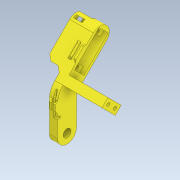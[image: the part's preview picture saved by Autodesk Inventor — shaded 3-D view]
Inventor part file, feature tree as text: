
AUTODESK INVENTOR PART (.ipt)
format: ipt  version: 2020 (Build 240168000, 168)  size: 848,384 bytes
history: native  units: mm
features: sketch x33, extrude x30, projected_geometry x17, reference x11, other x11, plane x4, chamfer x4, hole x3, split x2, boolean_combine x2, revolve x1, imported_body x1, fillet x1
ambient origin geometry x8: Origin, YZ Plane, XZ Plane, XY Plane, X Axis, Y Axis, Z Axis, Center Point
bodies: Solid1 (feature_tree), Solid2 (feature_tree), Solid3 (feature_tree), Solid4 (feature_tree), Solid5 (feature_tree), Solid6 (feature_tree)
feature tree (120):
  extrude  "Extrusion1"  Depth=70.0mm
  plane  "Work Plane1"
  extrude  "Extrusion2"  Depth=18.0mm
  extrude  "Extrusion3"  Depth=2.0mm TaperAngle=0.0deg
  extrude  "Extrusion4"  TaperAngle=0.0deg  [1 undecoded]
  extrude  "Extrusion5"  Depth=35.0mm TaperAngle=0.0deg
  extrude  "Extrusion12"  Depth=3.599976mm
  extrude  "Extrusion13"  Depth=0.15mm
  extrude  "Extrusion14"  Depth=0.15mm
  extrude  "Extrusion15"  Depth=15.9mm TaperAngle=0.0deg
  extrude  "Extrusion16"  Depth=5.0mm
  extrude  "Extrusion17"  Depth=53.0mm
  extrude  "Extrusion18"  Depth=37.3mm
  plane  "Work Plane2"
  extrude  "Extrusion19"  Depth=0.15mm
  hole  "Hole2"  [1 undecoded]
  plane  "Work Plane3"
  split  "Split1"
  extrude  "Extrusion20"  Depth=10.0mm
  extrude  "Extrusion21"  Depth=8.0mm
  extrude  "Extrusion22"  Depth=45.2mm TaperAngle=0.0deg
  plane  "Work Plane4"
  boolean_combine  "Combine1"
  split  "Split2"
  revolve  "Revolution1"  [1 undecoded]
  imported_body  "Base1"
  boolean_combine  "Combine2"
  hole  "Hole4"  [1 undecoded]
  extrude  "Extrusion30"  Depth=18.0mm
  extrude  "Extrusion31"  Depth=9.0mm
  extrude  "Extrusion33"  Depth=23.3mm
  extrude  "Extrusion34"  Depth=17.35mm TaperAngle=0.0deg
  chamfer  "Chamfer1"  Distance=10.0mm
  extrude  "Extrusion35"  Depth=3.0mm
  fillet  "Fillet3"  Radius=4.5mm
  extrude  "Extrusion36"  Depth=4.0mm
  extrude  "Extrusion37"  Depth=2.0mm
  extrude  "Extrusion38"  Depth=1.6mm TaperAngle=0.0deg
  extrude  "Extrusion39"  Depth=1.7mm TaperAngle=0.0deg
  extrude  "Extrusion40"  Depth=2.0mm
  chamfer  "Chamfer2"  Distance=12.899964mm
  extrude  "Extrusion42"  Depth=2.0mm
  extrude  "Extrusion43"  Depth=2.0mm
  extrude  "Extrusion48"  Depth=2.0mm
  extrude  "Extrusion49"  Depth=2.0mm
  chamfer  "Chamfer8"  Distance=30.143363mm
  chamfer  "Chamfer9"  Distance=124.5mm
  sketch  "Sketch1"  dims[d0=18.0mm d1=70.0mm]
  reference  "Reference1"
  sketch  "Sketch2"  dims[d2=70.0mm d3=18.0mm]
  reference  "Reference2"
  sketch  "Sketch3"  dims[d4=18.0mm d5=51.1mm d6=2.0mm d7=0.0mm d8=0.0mm]
  reference  "Reference3"
  reference  "Reference4"
  reference  "Reference5"
  reference  "Reference6"
  reference  "Reference7"
  reference  "Reference8"
  sketch  "Sketch4"  dims[d9=37.3mm d10=0.0mm]
  sketch  "Sketch5"  dims[d11=35.0mm d12=50.1mm d13=0.0mm]
  sketch  "Sketch12"  dims[d14=7.199887mm d15=3.599976mm]
  sketch  "Sketch14"  dims[d16=0.15mm d17=0.15mm]
  reference  "Reference12"
  reference  "Reference13"
  sketch  "Sketch15"  dims[d18=0.15mm d19=0.15mm]
  sketch  "Sketch16"  dims[d20=5.4mm d21=0.0mm d22=15.9mm d23=0.0mm]
  reference  "Reference14"
  sketch  "Sketch17"  dims[d24=5.0mm d25=0.0mm d78=3.85mm]
  sketch  "Sketch19"  dims[d79=10.925mm d80=53.0mm]
  sketch  "Sketch22"  dims[d81=53.0mm d82=37.3mm]
  projected_geometry  "Projected Loop1"
  sketch  "Sketch23"  dims[d83=40.0mm d84=0.0mm d86=0.15mm]
  sketch  "Sketch25"  dims[d87=0.15mm d88=4.0mm d89=0.0mm]
  sketch  "Sketch26"  dims[d90=20.0mm d91=0.0mm d92=10.0mm]
  sketch  "Sketch27"  dims[d93=4.0mm d94=0.0mm d95=8.0mm]
  sketch  "Sketch28"  dims[d96=18.0mm d97=45.2mm d98=0.0mm]
  sketch  "Sketch32"  dims[d99=12.7mm d100=0.3mm]
  projected_geometry  "Projected Loop2"
  projected_geometry  "Projected Loop3"
  sketch  "Sketch33"  dims[d101=12.7mm d102=0.3mm]
  hole  "Hole3"  [1 undecoded]
  sketch  "Sketch39"  dims[d103=10.0mm d104=0.0mm d109=18.0mm]
  projected_geometry  "Projected Loop15"
  projected_geometry  "Projected Loop16"
  projected_geometry  "Projected Loop17"
  sketch  "Sketch40"  dims[d111=31.0mm d112=9.0mm]
  projected_geometry  "Projected Loop18"
  sketch  "Sketch42"  dims[d113=9.0mm d114=23.3mm]
  projected_geometry  "Projected Loop20"
  sketch  "Sketch43"  dims[d115=23.3mm d116=17.35mm d117=0.0mm]
  projected_geometry  "Projected Loop21"
  projected_geometry  "Projected Loop22"
  sketch  "Sketch44"  dims[d118=15.0mm]
  sketch  "Sketch45"  dims[d119=4.0mm]
  projected_geometry  "Projected Loop23"
  sketch  "Sketch46"  dims[d120=8.0mm d121=10.0mm d122=0.0mm]
  sketch  "Sketch47"  dims[d132=3.0mm d133=3.0mm d134=4.5mm]
  projected_geometry  "Projected Loop24"
  sketch  "Sketch48"  dims[d135=4.5mm d136=4.0mm]
  sketch  "Sketch49"  dims[d137=4.0mm]
  projected_geometry  "Projected Loop25"
  sketch  "Sketch51"  dims[d138=3.0mm d139=6.0mm d140=4.0mm d141=2.0mm d142=90.0deg d143=56.75mm d144=0.0mm d146=0.765mm]
  projected_geometry  "Projected Loop27"
  sketch  "Sketch52"  dims[d147=1.6mm d148=0.0mm d149=1.6mm d150=0.0mm]
  projected_geometry  "Projected Loop28"
  sketch  "Sketch57"  dims[d151=0.765mm d152=1.7mm d153=0.0mm]
  projected_geometry  "Projected Loop33"
  sketch  "Sketch58"  dims[d167=45.0deg d170=3.4mm d171=6.0mm d172=4.0mm d173=2.0mm d174=90.0deg d175=8.0mm d176=0.0mm d234=1.309879mm d235=12.899964mm d236=16.829276mm d237=30.143363mm d238=6.142074mm d239=23.491994mm d240=30.143363mm d241=124.5mm d242=0.0mm d243=10.0mm d244=0.0mm d247=10.0mm d248=0.0mm d249=2.5mm d250=0.0mm d251=4.0mm d252=2.0mm d253=45.0deg d254=2.5mm d255=0.0mm d256=2.0mm d257=6.0mm d258=2.0mm d259=4.25mm d260=8.5mm d261=3.0mm d262=10.0mm d263=0.0mm d264=6.0mm d265=6.0mm d266=10.0mm d267=2.0mm d268=0.0mm d269=1.0mm d270=4.0mm d271=1.0mm d272=1.0mm d273=2.0mm d274=2.0mm d275=0.0mm d276=6.0mm d277=6.0mm d278=2.0mm d279=0.0mm d280=2.0mm d281=1.0mm d282=4.0mm d283=1.0mm d284=1.0mm d285=2.0mm d286=0.0mm d287=1.9mm d288=2.0mm d289=45.0deg d300=1.0mm d301=2.0mm d302=0.0mm d303=2.5mm d304=0.0mm d305=13.75mm d306=0.0mm d322=7.0mm d323=0.0mm d324=2.0mm d325=5.0mm d326=0.0mm d330=2.0mm d331=2.0mm d332=45.0deg d333=2.0mm d334=2.0mm d335=45.0deg d30=0.5mm d31=0.872665mm d32=0.5mm d33=0.872665mm d34=0.872665mm d35=0.5mm d36=0.872665mm]
  projected_geometry  "Projected Loop34"
  parser-record x3  (decoder bookkeeping rows leaked as tree rows — omitted from the tree; the rows remain in map.json)
  other  "Demo2.0004.iam"
  other  "Bearing:2"
  other  "Rolling bearing GB/T 7218-1995 Type FSN 70000-Z F 623-Z:1"
  other  "servo horn 1:1"
  other  "Assembly4.iam"
  other  "Tower Pro MG90S Micro servo:3"
  other  "Крышка корпуса:1"
  other  "Вал последний с чем то:1"
note: 5 required parameter values undecoded (feature->parameter linkage not recoverable at this tier; creation-order binding heuristic only, values carry confidence <= 0.55)
note: 3 file-system paths scrubbed to <path> (originals preserved in map.json)